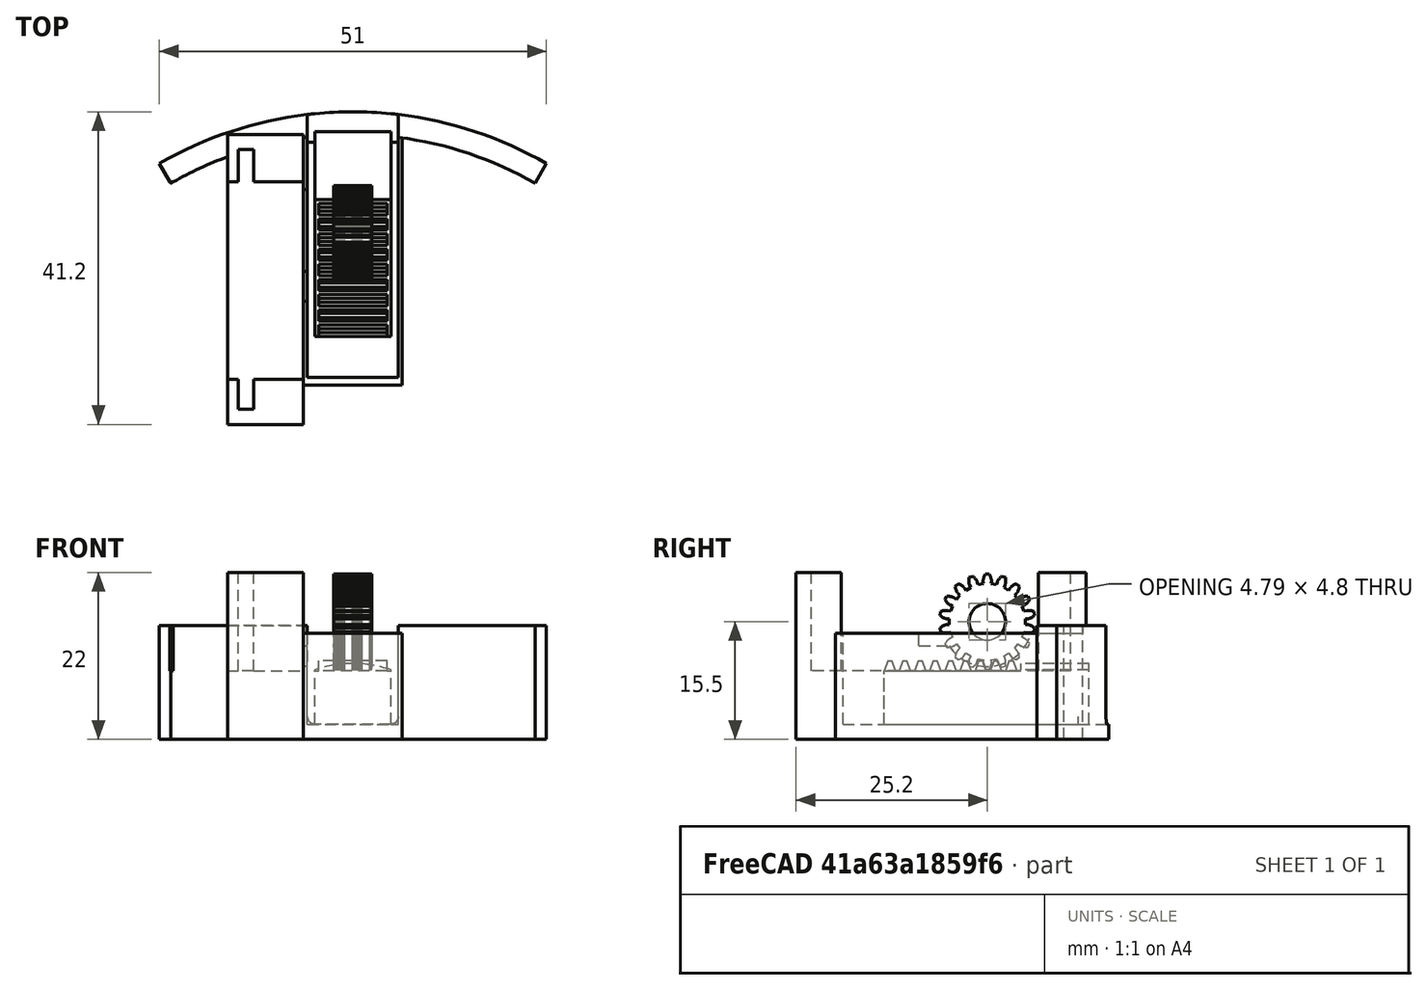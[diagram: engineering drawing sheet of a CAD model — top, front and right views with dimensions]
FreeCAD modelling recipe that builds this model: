
FCSTD DOCUMENT  (FreeCAD 0.16R4924 (Git))
Label: interior_servo_bay_v4p20yay
License: All rights reserved
LicenseURL: http://en.wikipedia.org/wiki/All_rights_reserved
objects: Part::Feature×11, Part::Box×11, Part::Cut×7, Part::MultiFuse×7, Part::Cylinder×4, Part::Extrusion×3, Part::Thickness×1, Mesh::Feature×1, Part::Fuse×1, Part::FeaturePython×1, Part::Prism×1, Part::MultiCommon×1
note: 48 computed .brp shape members not serialized (recipe doc carries the construction recipe); baked Part::Feature solids carry a one-line shape summary decoded from their .brp

FEATURE [Part::Cylinder] Cylinder  label="bottle_wall"
  Angle = 60
  Height = 15
  Placement = pos=(8.5,-7,0) rot=(0,0,1;1.0472rad)
  Radius = 51
FEATURE [Part::Cylinder] Cylinder001  label="bottle_wall001"
  Angle = 60
  Height = 15
  Placement = pos=(8.5,-7,0) rot=(0,0,1;1.0472rad)
  Radius = 48
FEATURE [Part::Cut] Cut  label="bottle_wall_composite"
  Base = -> Cylinder
  Placement = pos=(0,-2,0) rot=(0,0,1;0rad)
  Tool = -> Cylinder001
FEATURE [Part::Feature] Common_cs  label="pin_cs"
  Placement = pos=(3.5,35,2) rot=(0,0,1;0rad)
  shape: bbox 10 x 2e-07 x 8 mm, 0 faces, 0 solids (baked)
FEATURE [Part::Extrusion] Extrude
  Base = -> Common_cs
  Dir = (0,5,0)
  Solid = true
FEATURE [Part::Thickness] Thickness
  Faces = -> Extrude [Face7]
  Intersection = false
  Join = 0
  Mode = 0
  SelfIntersection = false
  Value = 1
FEATURE [Part::Feature] Common_cs001  label="pin_cs001"
  Placement = pos=(3.5,35,2) rot=(0,0,1;0rad)
  shape: bbox 10 x 2e-07 x 8 mm, 0 faces, 0 solids (baked)
FEATURE [Part::Extrusion] Extrude001
  Base = -> Common_cs001
  Dir = (0,5,0)
  Solid = true
FEATURE [Part::MultiFuse] Fusion  label="bolt_bottle_side_opening"
  Placement = pos=(0,-7,1) rot=(0,0,1;0rad)
  Shapes = -> [Thickness,Extrude,Extrude001]
FEATURE [Part::Box] Box  label="pullBay"
  Height = 15
  Length = 12
  Placement = pos=(2.5,7,2) rot=(0,0,1;0rad)
  Width = 31
FEATURE [Part::Box] Box001  label="Case"
  Height = 14
  Length = 13
  Placement = pos=(2,6,0) rot=(0,0,1;0rad)
  Width = 34
FEATURE [Part::Cut] Cut001  label="cut bay from case"
  Base = -> Box001
  Tool = -> Box
FEATURE [Part::MultiFuse] Fusion001  label="wall plus case"
  Shapes = -> [Cut,Cut001]
FEATURE [Part::Cut] Cut002  label="hole cut out of case"
  Base = -> Fusion001
  Tool = -> Fusion
FEATURE [Mesh::Feature] Mesh  label="servo_motor_2"
  Placement = pos=(33.6,-52,22) rot=(0,0,-1;1.5708rad)
FEATURE [Part::Fuse] union  label="pinion"
FEATURE [Part::FeaturePython] RefineLinearExtrude  # WARN: FeaturePython — macro-defined, semantics opaque (R4)
  Base = -> union
FEATURE [Part::Extrusion] LinearExtrude
  Base = -> RefineLinearExtrude
  Dir = (0,0,5)
  Solid = true
FEATURE [Part::Prism] prism
  Circumradius = 2.4
  Height = 7
  Placement = pos=(0,0,-1) rot=(0,0,1;0rad)
  Polygon = 50
FEATURE [Part::Cut] difference  label="pinion_final"
  Base = -> LinearExtrude
  Placement = pos=(6,26,15.5) rot=(0,1,0;1.5708rad)
  Tool = -> prism
FEATURE [Part::Cylinder] Cylinder002  label="rounded_top"
  Angle = 360
  Height = 40
  Placement = pos=(5,35,-7) rot=(1,0,0;1.5708rad)
  Radius = 15
FEATURE [Part::Box] Box005  label="pin"
  Height = 8
  Length = 10
  Width = 27
FEATURE [Part::MultiCommon] Common  label="rounded pin"
  Shapes = -> [Cylinder002,Box005]
FEATURE [Part::Box] Box006  label="flat_top"
  Height = 10
  Length = 10
  Placement = pos=(0,0,7) rot=(0,0,1;0rad)
  Width = 18
FEATURE [Part::Cut] Cut005
  Base = -> Common
  Placement = pos=(0,11,0) rot=(0,0,1;0rad)
  Tool = -> Box006
FEATURE [Part::Box] cube
  Height = 5
  Length = 18
  Placement = pos=(-12,-4.5,-2.5) rot=(0,0,1;0rad)
  Width = 9
FEATURE [Part::Feature] polyhedron
  Placement = pos=(-11.2451,0,2.5) rot=(0,0,1;0rad)
  shape: bbox 1.51 x 9 x 1.337 mm, 6 faces (baked)
FEATURE [Part::Feature] polyhedron001
  Placement = pos=(-9.24512,0,2.5) rot=(0,0,1;0rad)
  shape: bbox 1.51 x 9 x 1.337 mm, 6 faces (baked)
FEATURE [Part::Feature] polyhedron002
  Placement = pos=(-7.24512,0,2.5) rot=(0,0,1;0rad)
  shape: bbox 1.51 x 9 x 1.337 mm, 6 faces (baked)
FEATURE [Part::Feature] polyhedron003
  Placement = pos=(-5.24512,0,2.5) rot=(0,0,1;0rad)
  shape: bbox 1.51 x 9 x 1.337 mm, 6 faces (baked)
FEATURE [Part::Feature] polyhedron004
  Placement = pos=(-3.24512,0,2.5) rot=(0,0,1;0rad)
  shape: bbox 1.51 x 9 x 1.337 mm, 6 faces (baked)
FEATURE [Part::Feature] polyhedron005
  Placement = pos=(-1.24512,0,2.5) rot=(0,0,1;0rad)
  shape: bbox 1.51 x 9 x 1.337 mm, 6 faces (baked)
FEATURE [Part::Feature] polyhedron006
  Placement = pos=(0.754882,0,2.5) rot=(0,0,1;0rad)
  shape: bbox 1.51 x 9 x 1.337 mm, 6 faces (baked)
FEATURE [Part::Feature] polyhedron007
  Placement = pos=(2.75488,0,2.5) rot=(0,0,1;0rad)
  shape: bbox 1.51 x 9 x 1.337 mm, 6 faces (baked)
FEATURE [Part::Feature] polyhedron008
  Placement = pos=(4.75488,0,2.5) rot=(0,0,1;0rad)
  shape: bbox 1.51 x 9 x 1.337 mm, 6 faces (baked)
FEATURE [Part::MultiFuse] Fusion003  label="rack"
  Placement = pos=(5,23,4.5) rot=(0,0,1;1.5708rad)
  Shapes = -> [cube,polyhedron002,polyhedron003,polyhedron004,polyhedron005,polyhedron,polyhedron007,polyhedron001,polyhedron006,polyhedron008]
FEATURE [Part::MultiFuse] Fusion004  label="pin_3p2"
  Placement = pos=(3.5,1.4,2) rot=(0,0,1;0rad)
  Shapes = -> [Fusion003,Cut005]
FEATURE [Part::Box] Box007  label="mount"
  Height = 22
  Length = 10
  Placement = pos=(-8,2,0) rot=(0,0,1;0rad)
  Width = 37
FEATURE [Part::Box] Box008  label="Cube"
  Height = 13
  Length = 35
  Placement = pos=(-42,1.5,-2) rot=(0,0,1;0rad)
  Width = 2
FEATURE [Part::Box] Box009  label="Cube001"
  Height = 13
  Length = 26
  Placement = pos=(-37.75,-13.6,-2) rot=(0,0,1;0rad)
  Width = 23.7
FEATURE [Part::Box] Box010  label="Cube002"
  Height = 7
  Length = 10
  Placement = pos=(-32,3.3,1.3) rot=(0,0,1;0rad)
  Width = 10
FEATURE [Part::Cylinder] Cylinder003
  Angle = 360
  Height = 6
  Placement = pos=(-31,14.3,4.6) rot=(1,0,0;1.5708rad)
  Radius = 6
FEATURE [Part::MultiFuse] Fusion005  label="simple_servo_rev_eng"
  Placement = pos=(-8.1,-5,11) rot=(0,0,-1;1.5708rad)
  Shapes = -> [Box008,Box010,Cylinder003,Box009]
FEATURE [Part::MultiFuse] Fusion006
  Shapes = -> [Box007,Cut002]
FEATURE [Part::Cut] Cut006
  Base = -> Fusion006
  Tool = -> Fusion005
FEATURE [Part::Box] Box011  label="bracket extention"
  Height = 22
  Length = 10
  Placement = pos=(-8,0.8,0) rot=(0,0,1;0rad)
  Width = 2
FEATURE [Part::MultiFuse] Fusion007
  Shapes = -> [Cut006,Box011]
FEATURE [Part::Box] Box012  label="Cube003"
  Height = 8
  Length = 12
  Placement = pos=(2.5,36,10) rot=(0,0,1;0rad)
  Width = 7
FEATURE [Part::Cut] Cut007
  Base = -> Fusion007
  Tool = -> Box012
